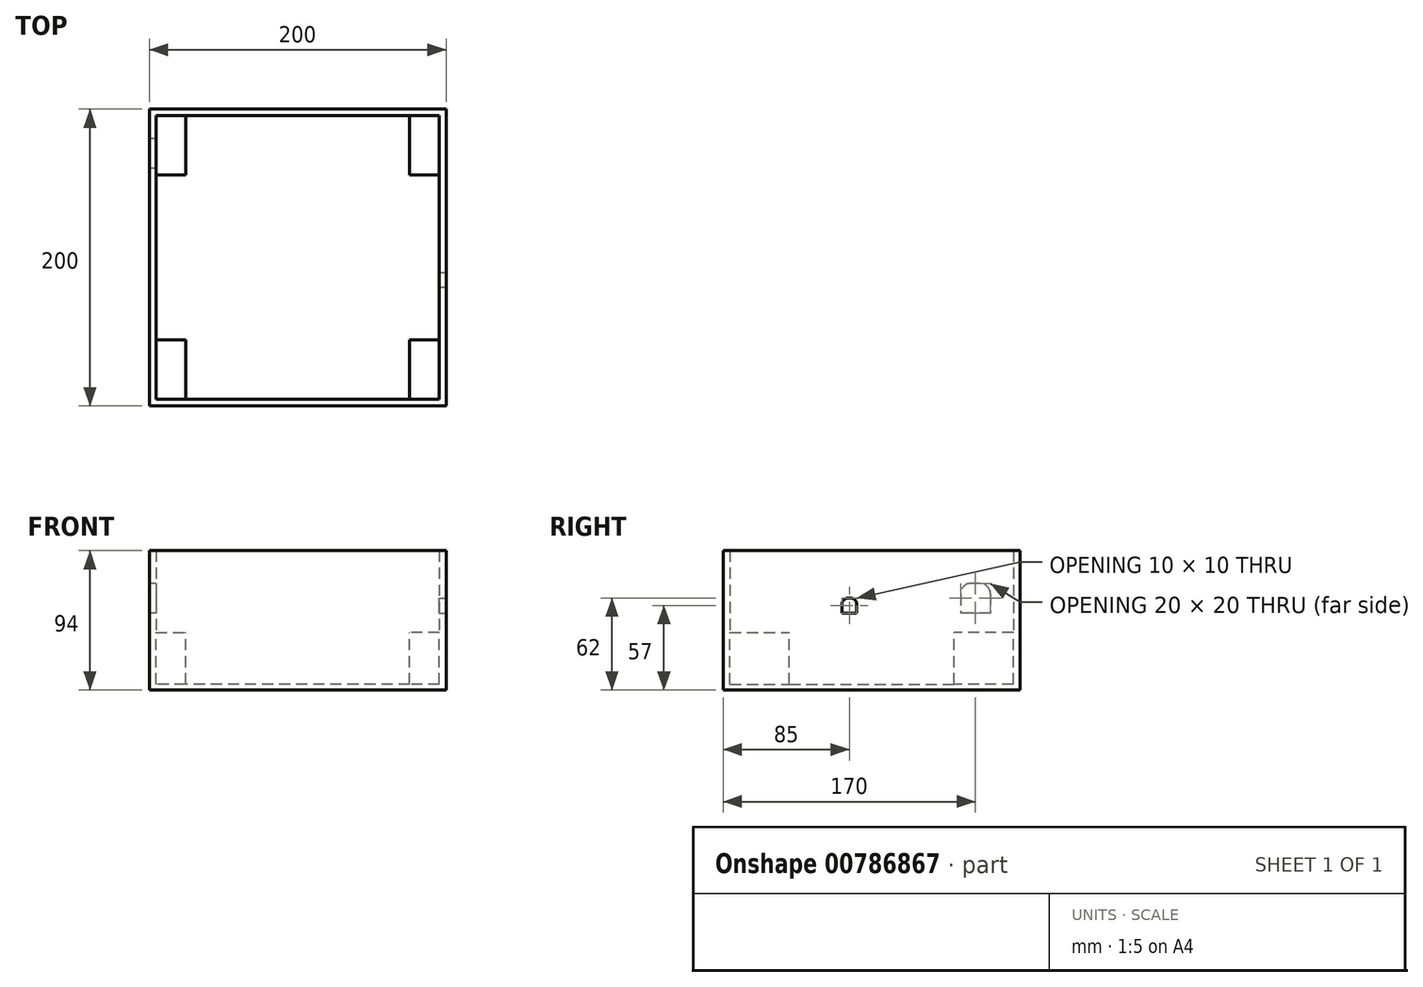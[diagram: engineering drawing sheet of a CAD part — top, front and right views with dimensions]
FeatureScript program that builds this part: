
annotation { "Feature Type Name" : "Feature", "Feature Type Description" : "" }
export const myFeature = defineFeature(function(context is Context, id is Id, definition is map)
    precondition{}
    {
        {
            var Q0;
            Q0=qCreatedBy(makeId("Top.planeOp"),FACE);
            var sketch = newSketch(context, id + "F0", { "sketchPlane" : qUnion([Q0])});
            skLineSegment(sketch, "E0.bottom", {"start": v(95.5, -95.5) * mm, "end": v(-95.5, -95.5) * mm});
            skLineSegment(sketch, "E0.top", {"start": v(95.5, 95.5) * mm, "end": v(-95.5, 95.5) * mm});
            skLineSegment(sketch, "E0.left", {"start": v(95.5, -95.5) * mm, "end": v(95.5, 95.5) * mm});
            skLineSegment(sketch, "E0.right", {"start": v(-95.5, -95.5) * mm, "end": v(-95.5, 95.5) * mm});
            skPoint(sketch, "E0.middle", {"position": v(0, 0) * mm});
            skSolve(sketch);
        }
        {
            var Q0;
            Q0=makeQuery(id+"F0.imprint","IMPRINT",FACE,{"disambiguationData":[TD([[makeQuery(id+"F0.imprint","IMPRINT",EDGE,{"derivedFrom":sQuery(id+"F0.wireOp",EDGE,"E0.bottom")}),-1.0]])]});
            var sketch = newSketch(context, id + "F1", { "sketchPlane" : qUnion([Q0])});
            skLineSegment(sketch, "E1.bottom", {"start": v(100, -100) * mm, "end": v(-100, -100) * mm});
            skLineSegment(sketch, "E1.top", {"start": v(100, 100) * mm, "end": v(-100, 100) * mm});
            skLineSegment(sketch, "E1.left", {"start": v(100, -100) * mm, "end": v(100, 100) * mm});
            skLineSegment(sketch, "E1.right", {"start": v(-100, -100) * mm, "end": v(-100, 100) * mm});
            skPoint(sketch, "E1.middle", {"position": v(0, 0) * mm});
            skSolve(sketch);
        }
        {
            var Q0;
            Q0=makeQuery(id+"F1.imprint","IMPRINT",FACE,{"disambiguationData":[TD([[makeQuery(id+"F1.imprint","IMPRINT",EDGE,{"derivedFrom":sQuery(id+"F1.wireOp",EDGE,"E1.bottom")}),-1.0]])]});
            extrude(context, id + "F2", {"entities" : qUnion([Q0]), "depth" : 94 * mm, "offsetDistance" : 25 * mm});
        }
        {
            var Q0;
            Q0=makeQuery(id+"F0.imprint","IMPRINT",FACE,{"disambiguationData":[TD([[makeQuery(id+"F0.imprint","IMPRINT",EDGE,{"derivedFrom":sQuery(id+"F0.wireOp",EDGE,"E0.bottom")}),-1.0]])]});
            extrude(context, id + "F3", {"entities" : qUnion([Q0]), "operationType" : NewBodyOperationType.ADD, "depth" : 4 * mm, "offsetDistance" : 25 * mm});
        }
        {
            var Q0;
            Q0=makeQuery(id+"F3.opExtrude","CAP_FACE",FACE,{"disambiguationData":[OSD([sQuery(id+"F0.wireOp",EDGE,"E0.bottom"),sQuery(id+"F0.wireOp",EDGE,"E0.top"),sQuery(id+"F0.wireOp",EDGE,"E0.left"),sQuery(id+"F0.wireOp",EDGE,"E0.right")])],"isStart":false});
            cPlane(context, id + "F4", {"entities" : qUnion([Q0]), "cplaneType" : CPlaneType.OFFSET, "offset" : 35 * mm, "width" : 150 * mm, "height" : 150 * mm});
        }
        {
            var Q0;
            Q0=qCreatedBy(id+"F4.planeOp",FACE);
            var sketch = newSketch(context, id + "F5", { "sketchPlane" : qUnion([Q0])});
            skLineSegment(sketch, "E2.bottom", {"start": v(-95.5, -95.5) * mm, "end": v(-75.5, -95.5) * mm});
            skLineSegment(sketch, "E2.top", {"start": v(-95.5, -55.5) * mm, "end": v(-75.5, -55.5) * mm});
            skLineSegment(sketch, "E2.left", {"start": v(-95.5, -95.5) * mm, "end": v(-95.5, -55.5) * mm});
            skLineSegment(sketch, "E2.right", {"start": v(-75.5, -95.5) * mm, "end": v(-75.5, -55.5) * mm});
            skSolve(sketch);
        }
        {
            var Q0;
            Q0=qCreatedBy(id+"F4.planeOp",FACE);
            var sketch = newSketch(context, id + "F6", { "sketchPlane" : qUnion([Q0])});
            skLineSegment(sketch, "E3.bottom", {"start": v(-75.5, 95.5) * mm, "end": v(-95.5, 95.5) * mm});
            skLineSegment(sketch, "E3.top", {"start": v(-75.5, 55.5) * mm, "end": v(-95.5, 55.5) * mm});
            skLineSegment(sketch, "E3.left", {"start": v(-75.5, 95.5) * mm, "end": v(-75.5, 55.5) * mm});
            skLineSegment(sketch, "E3.right", {"start": v(-95.5, 95.5) * mm, "end": v(-95.5, 55.5) * mm});
            skSolve(sketch);
        }
        {
            var Q0;
            Q0=qCreatedBy(id+"F4.planeOp",FACE);
            var sketch = newSketch(context, id + "F7", { "sketchPlane" : qUnion([Q0])});
            skLineSegment(sketch, "E4.bottom", {"start": v(95.5, 95.5) * mm, "end": v(75.5, 95.5) * mm});
            skLineSegment(sketch, "E4.top", {"start": v(95.5, 55.5) * mm, "end": v(75.5, 55.5) * mm});
            skLineSegment(sketch, "E4.left", {"start": v(95.5, 95.5) * mm, "end": v(95.5, 55.5) * mm});
            skLineSegment(sketch, "E4.right", {"start": v(75.5, 95.5) * mm, "end": v(75.5, 55.5) * mm});
            skSolve(sketch);
        }
        {
            var Q0;
            Q0=qCreatedBy(id+"F4.planeOp",FACE);
            var sketch = newSketch(context, id + "F8", { "sketchPlane" : qUnion([Q0])});
            skLineSegment(sketch, "E5.bottom", {"start": v(95.5, -95.5) * mm, "end": v(75.5, -95.5) * mm});
            skLineSegment(sketch, "E5.top", {"start": v(95.5, -55.5) * mm, "end": v(75.5, -55.5) * mm});
            skLineSegment(sketch, "E5.left", {"start": v(95.5, -95.5) * mm, "end": v(95.5, -55.5) * mm});
            skLineSegment(sketch, "E5.right", {"start": v(75.5, -95.5) * mm, "end": v(75.5, -55.5) * mm});
            skSolve(sketch);
        }
        {
            var Q0;
            Q0=makeQuery(id+"F6.imprint","IMPRINT",FACE,{"disambiguationData":[TD([[makeQuery(id+"F6.imprint","IMPRINT",EDGE,{"derivedFrom":sQuery(id+"F6.wireOp",EDGE,"E3.bottom")}),1.0]])]});
            extrude(context, id + "F9", {"entities" : qUnion([Q0]), "operationType" : NewBodyOperationType.ADD, "oppositeDirection" : true, "depth" : 35 * mm, "offsetDistance" : 25 * mm});
        }
        {
            var Q0;
            Q0=makeQuery(id+"F5.imprint","IMPRINT",FACE,{"disambiguationData":[TD([[makeQuery(id+"F5.imprint","IMPRINT",EDGE,{"derivedFrom":sQuery(id+"F5.wireOp",EDGE,"E2.bottom")}),1.0]])]});
            extrude(context, id + "F10", {"entities" : qUnion([Q0]), "operationType" : NewBodyOperationType.ADD, "oppositeDirection" : true, "depth" : 35 * mm, "offsetDistance" : 25 * mm});
        }
        {
            var Q0;
            Q0=makeQuery(id+"F8.imprint","IMPRINT",FACE,{"disambiguationData":[TD([[makeQuery(id+"F8.imprint","IMPRINT",EDGE,{"derivedFrom":sQuery(id+"F8.wireOp",EDGE,"E5.bottom")}),-1.0]])]});
            extrude(context, id + "F11", {"entities" : qUnion([Q0]), "operationType" : NewBodyOperationType.ADD, "oppositeDirection" : true, "depth" : 35 * mm, "offsetDistance" : 25 * mm});
        }
        {
            var Q0;
            Q0=makeQuery(id+"F7.imprint","IMPRINT",FACE,{"disambiguationData":[TD([[makeQuery(id+"F7.imprint","IMPRINT",EDGE,{"derivedFrom":sQuery(id+"F7.wireOp",EDGE,"E4.bottom")}),1.0]])]});
            extrude(context, id + "F12", {"entities" : qUnion([Q0]), "operationType" : NewBodyOperationType.ADD, "oppositeDirection" : true, "depth" : 35 * mm, "offsetDistance" : 25 * mm});
        }
        {
            var Q0;
            Q0=makeQuery(id+"F2.opExtrude","SWEPT_FACE",FACE,{"disambiguationData":[OSD([sQuery(id+"F1.wireOp",EDGE,"E1.right")])]});
            var sketch = newSketch(context, id + "F13", { "sketchPlane" : qUnion([Q0])});
            skLineSegment(sketch, "E6.bottom", {"start": v(-73, 72) * mm, "end": v(-67, 72) * mm});
            skLineSegment(sketch, "E6.top", {"start": v(-80, 52) * mm, "end": v(-60, 52) * mm});
            skLineSegment(sketch, "E6.left", {"start": v(-80, 65) * mm, "end": v(-80, 52) * mm});
            skLineSegment(sketch, "E6.right", {"start": v(-60, 65) * mm, "end": v(-60, 52) * mm});
            skPoint(sketch, "E7.visualSharp", {"position": v(-80, 72) * mm});
            skArc(sketch, "E7.filletArc", {"start": v(-73, 72) * mm, "mid": v(-77.95, 69.95) * mm, "end": v(-80, 65) * mm});
            skPoint(sketch, "E8.visualSharp", {"position": v(-60, 72) * mm});
            skArc(sketch, "E8.filletArc", {"start": v(-60, 65) * mm, "mid": v(-62.05, 69.95) * mm, "end": v(-67, 72) * mm});
            skSolve(sketch);
        }
        {
            var Q0;
            Q0=makeQuery(id+"F13.imprint","IMPRINT",FACE,{"disambiguationData":[TD([[makeQuery(id+"F13.imprint","IMPRINT",EDGE,{"derivedFrom":sQuery(id+"F13.wireOp",EDGE,"E6.bottom")}),-1.0]])]});
            extrude(context, id + "F14", {"entities" : qUnion([Q0]), "operationType" : NewBodyOperationType.REMOVE, "oppositeDirection" : true, "depth" : 25 * mm, "offsetDistance" : 25 * mm});
        }
        {
            var Q0;
            Q0=makeQuery(id+"F2.opExtrude","SWEPT_FACE",FACE,{"disambiguationData":[OSD([sQuery(id+"F1.wireOp",EDGE,"E1.left")])]});
            var sketch = newSketch(context, id + "F15", { "sketchPlane" : qUnion([Q0])});
            skLineSegment(sketch, "E9.bottom", {"start": v(-16, 62) * mm, "end": v(-14, 62) * mm});
            skLineSegment(sketch, "E9.top", {"start": v(-20, 52) * mm, "end": v(-10, 52) * mm});
            skLineSegment(sketch, "E9.left", {"start": v(-20, 58) * mm, "end": v(-20, 52) * mm});
            skLineSegment(sketch, "E9.right", {"start": v(-10, 58) * mm, "end": v(-10, 52) * mm});
            skPoint(sketch, "E10.visualSharp", {"position": v(-20, 62) * mm});
            skArc(sketch, "E10.filletArc", {"start": v(-16, 62) * mm, "mid": v(-18.83, 60.83) * mm, "end": v(-20, 58) * mm});
            skPoint(sketch, "E11.visualSharp", {"position": v(-10, 62) * mm});
            skArc(sketch, "E11.filletArc", {"start": v(-10, 58) * mm, "mid": v(-11.17, 60.83) * mm, "end": v(-14, 62) * mm});
            skSolve(sketch);
        }
        {
            var Q0;
            Q0 = qSketchRegion(id + "F15", true);
            extrude(context, id + "F16", {"entities" : qUnion([Q0]), "operationType" : NewBodyOperationType.REMOVE, "oppositeDirection" : true, "depth" : 25 * mm, "offsetDistance" : 25 * mm});
        }
    });
